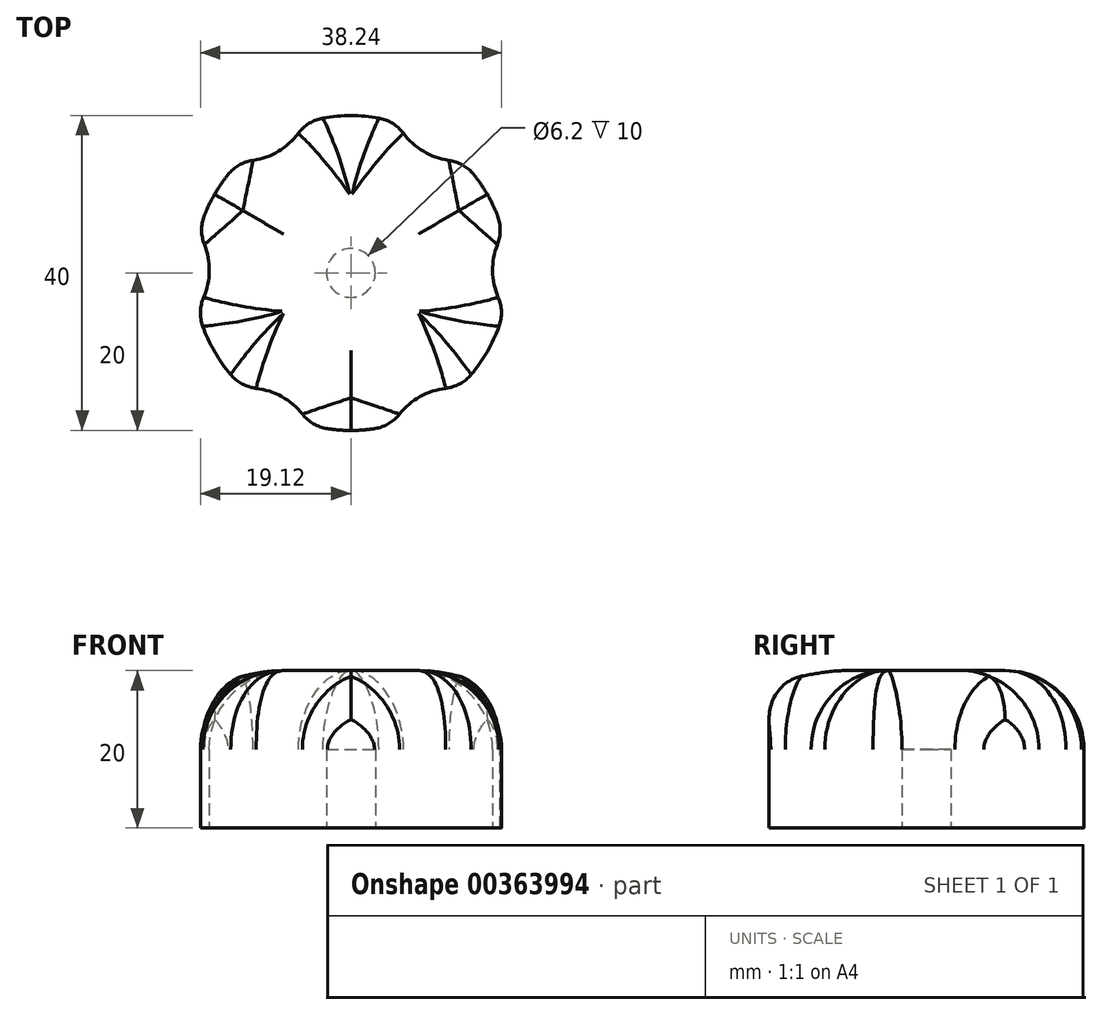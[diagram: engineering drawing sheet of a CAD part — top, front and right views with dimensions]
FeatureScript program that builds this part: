
annotation { "Feature Type Name" : "Feature", "Feature Type Description" : "" }
export const myFeature = defineFeature(function(context is Context, id is Id, definition is map)
    precondition{}
    {
        {
            var Q0;
            Q0=qCreatedBy(makeId("Top.planeOp"),FACE);
            var sketch = newSketch(context, id + "F0", { "sketchPlane" : qUnion([Q0])});
            skArc(sketch, "E0", {"start": v(19.35, 5.06) * mm, "mid": v(0, 20) * mm, "end": v(-19.35, 5.06) * mm});
            skArc(sketch, "E1", {"start": v(19.35, 5.06) * mm, "mid": v(18, 0.25) * mm, "end": v(19.48, -4.52) * mm});
            skArc(sketch, "E2.MirrorCS", {"start": v(-19.35, 5.06) * mm, "mid": v(-18, 0.25) * mm, "end": v(-19.48, -4.52) * mm});
            skArc(sketch, "E3.trimOffspring", {"start": v(-19.48, -4.52) * mm, "mid": v(0, -20) * mm, "end": v(19.48, -4.52) * mm});
            skArc(sketch, "E4.1.0", {"start": v(14.06, 14.22) * mm, "mid": v(9.21, 15.46) * mm, "end": v(5.82, 19.13) * mm});
            skArc(sketch, "E4.2.0", {"start": v(5.29, -19.29) * mm, "mid": v(8.78, -15.7) * mm, "end": v(13.66, -14.61) * mm});
            skLineSegment(sketch, "E4.anchor1", {"start": v(0, 0) * mm, "end": v(-26.79, 0.37) * mm, "construction": true});
            skLineSegment(sketch, "E4.anchor2", {"start": v(0, 0) * mm, "end": v(13.07, -23.38) * mm, "construction": true});
            skArc(sketch, "E5.MirrorCS", {"start": v(-14.06, 14.22) * mm, "mid": v(-9.21, 15.46) * mm, "end": v(-5.82, 19.13) * mm});
            skArc(sketch, "E6.MirrorCS", {"start": v(-5.29, -19.29) * mm, "mid": v(-8.78, -15.7) * mm, "end": v(-13.66, -14.61) * mm});
            skSolve(sketch);
        }
        {
            var Q0;
            Q0=makeQuery(id+"F0.imprint","IMPRINT",FACE,{"disambiguationData":[TD([[makeQuery(id+"F0.imprint","IMPRINT",EDGE,{"derivedFrom":sQuery(id+"F0.wireOp",EDGE,"E0")}),1.0]])]});
            extrude(context, id + "F1", {"entities" : qUnion([Q0]), "depth" : 20 * mm});
        }
        {
            var Q0;
            Q0=makeQuery(id+"F1.opExtrude","CAP_FACE",FACE,{"disambiguationData":[OSD([sQuery(id+"F0.wireOp",EDGE,"E0")])],"isStart":true});
            var sketch = newSketch(context, id + "F2", { "sketchPlane" : qUnion([Q0])});
            skCircle(sketch, "E7", {"center": v(0, 0) * mm, "radius": 3.1 * mm});
            skSolve(sketch);
        }
        {
            var Q0;
            Q0 = qSketchRegion(id + "F2", true);
            extrude(context, id + "F3", {"entities" : qUnion([Q0]), "operationType" : NewBodyOperationType.REMOVE, "oppositeDirection" : true, "depth" : 10 * mm});
        }
        {
            var Q0;
            Q0=makeQuery(id+"F1.opExtrude","CAP_FACE",FACE,{"disambiguationData":[OSD([sQuery(id+"F0.wireOp",EDGE,"E0"),sQuery(id+"F0.wireOp",EDGE,"E1"),sQuery(id+"F0.wireOp",EDGE,"E2.MirrorCS"),sQuery(id+"F0.wireOp",EDGE,"E3.trimOffspring"),sQuery(id+"F0.wireOp",EDGE,"E4.1.0"),sQuery(id+"F0.wireOp",EDGE,"E4.2.0"),sQuery(id+"F0.wireOp",EDGE,"E5.MirrorCS"),sQuery(id+"F0.wireOp",EDGE,"E6.MirrorCS")])],"isStart":false});
            fillet(context, id + "F4", {"entities" : qUnion([Q0]), "radius" : 10 * mm, "tangentPropagation" : true, "allowEdgeOverflow" : false});
        }
        {
            var Q0;
            Q0=makeQuery(id+"F1.opExtrude","SWEPT_EDGE",EDGE,{"disambiguationData":[OSD([sQuery(id+"F0.wireOp",EDGE,"E1"),sQuery(id+"F0.wireOp",EDGE,"E3.trimOffspring")])]});
            var Q1;
            {var subQ0=sQuery(id+"F0.wireOp",EDGE,"E4.2.0");var subQ1=sQuery(id+"F0.wireOp",EDGE,"E3.trimOffspring");Q1=makeQuery(id+"F1.opExtrude","SWEPT_EDGE",EDGE,{"disambiguationData":[OSD([subQ1,subQ0]),TDD([makeQuery(id+"F0.imprint","INTERSECT",VERTEX,{"disambiguationData":[OD(1.0)],"derivedFrom":[subQ1,subQ0]})])]});}
            var Q2;
            {var subQ0=sQuery(id+"F0.wireOp",EDGE,"E6.MirrorCS");var subQ1=sQuery(id+"F0.wireOp",EDGE,"E3.trimOffspring");Q2=makeQuery(id+"F1.opExtrude","SWEPT_EDGE",EDGE,{"disambiguationData":[OSD([subQ1,subQ0]),TDD([makeQuery(id+"F0.imprint","INTERSECT",VERTEX,{"disambiguationData":[OD(0.0)],"derivedFrom":[subQ1,subQ0]})])]});}
            var Q3;
            {var subQ0=sQuery(id+"F0.wireOp",EDGE,"E4.2.0");var subQ1=sQuery(id+"F0.wireOp",EDGE,"E3.trimOffspring");Q3=makeQuery(id+"F1.opExtrude","SWEPT_EDGE",EDGE,{"disambiguationData":[OSD([subQ1,subQ0]),TDD([makeQuery(id+"F0.imprint","INTERSECT",VERTEX,{"disambiguationData":[OD(0.0)],"derivedFrom":[subQ1,subQ0]})])]});}
            var Q4;
            {var subQ0=sQuery(id+"F0.wireOp",EDGE,"E6.MirrorCS");var subQ1=sQuery(id+"F0.wireOp",EDGE,"E3.trimOffspring");Q4=makeQuery(id+"F1.opExtrude","SWEPT_EDGE",EDGE,{"disambiguationData":[OSD([subQ1,subQ0]),TDD([makeQuery(id+"F0.imprint","INTERSECT",VERTEX,{"disambiguationData":[OD(1.0)],"derivedFrom":[subQ1,subQ0]})])]});}
            var Q5;
            Q5=makeQuery(id+"F1.opExtrude","SWEPT_EDGE",EDGE,{"disambiguationData":[OSD([sQuery(id+"F0.wireOp",EDGE,"E2.MirrorCS"),sQuery(id+"F0.wireOp",EDGE,"E3.trimOffspring")])]});
            var Q6;
            Q6=makeQuery(id+"F1.opExtrude","SWEPT_EDGE",EDGE,{"disambiguationData":[OSD([sQuery(id+"F0.wireOp",EDGE,"E0"),sQuery(id+"F0.wireOp",EDGE,"E2.MirrorCS")])]});
            var Q7;
            {var subQ0=sQuery(id+"F0.wireOp",EDGE,"E5.MirrorCS");var subQ1=sQuery(id+"F0.wireOp",EDGE,"E0");Q7=makeQuery(id+"F1.opExtrude","SWEPT_EDGE",EDGE,{"disambiguationData":[OSD([subQ1,subQ0]),TDD([makeQuery(id+"F0.imprint","INTERSECT",VERTEX,{"disambiguationData":[OD(0.0)],"derivedFrom":[subQ1,subQ0]})])]});}
            var Q8;
            {var subQ0=sQuery(id+"F0.wireOp",EDGE,"E5.MirrorCS");var subQ1=sQuery(id+"F0.wireOp",EDGE,"E0");Q8=makeQuery(id+"F1.opExtrude","SWEPT_EDGE",EDGE,{"disambiguationData":[OSD([subQ1,subQ0]),TDD([makeQuery(id+"F0.imprint","INTERSECT",VERTEX,{"disambiguationData":[OD(1.0)],"derivedFrom":[subQ1,subQ0]})])]});}
            var Q9;
            {var subQ0=sQuery(id+"F0.wireOp",EDGE,"E4.1.0");var subQ1=sQuery(id+"F0.wireOp",EDGE,"E0");Q9=makeQuery(id+"F1.opExtrude","SWEPT_EDGE",EDGE,{"disambiguationData":[OSD([subQ1,subQ0]),TDD([makeQuery(id+"F0.imprint","INTERSECT",VERTEX,{"disambiguationData":[OD(1.0)],"derivedFrom":[subQ1,subQ0]})])]});}
            var Q10;
            {var subQ0=sQuery(id+"F0.wireOp",EDGE,"E4.1.0");var subQ1=sQuery(id+"F0.wireOp",EDGE,"E0");Q10=makeQuery(id+"F1.opExtrude","SWEPT_EDGE",EDGE,{"disambiguationData":[OSD([subQ1,subQ0]),TDD([makeQuery(id+"F0.imprint","INTERSECT",VERTEX,{"disambiguationData":[OD(0.0)],"derivedFrom":[subQ1,subQ0]})])]});}
            var Q11;
            Q11=makeQuery(id+"F1.opExtrude","SWEPT_EDGE",EDGE,{"disambiguationData":[OSD([sQuery(id+"F0.wireOp",EDGE,"E0"),sQuery(id+"F0.wireOp",EDGE,"E1")])]});
            fillet(context, id + "F5", {"entities" : qUnion([Q0, Q1, Q2, Q3, Q4, Q5, Q6, Q7, Q8, Q9, Q10, Q11]), "radius" : 5 * mm, "tangentPropagation" : true, "allowEdgeOverflow" : false});
        }
    });
